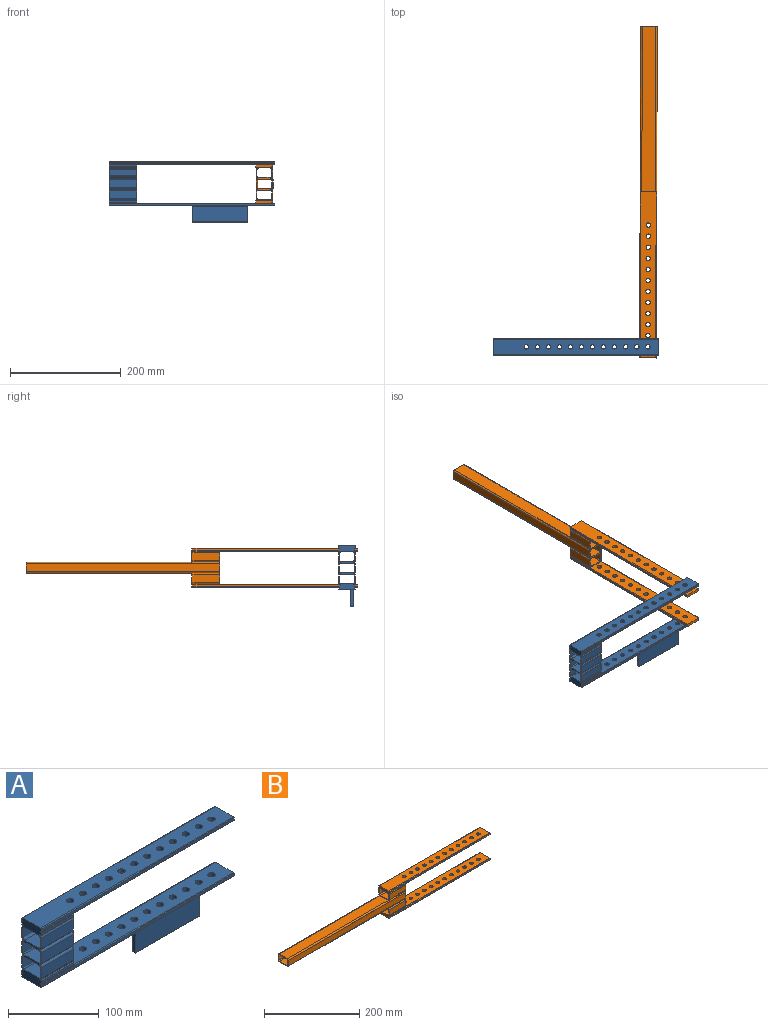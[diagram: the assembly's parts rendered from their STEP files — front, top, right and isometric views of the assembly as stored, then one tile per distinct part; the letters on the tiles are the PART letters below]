
ASSEMBLY  parts=2 mates=1
PART A: 111 faces, bbox 300x30x110 mm
  f0: cylinder r=1.5mm len=50mm, axis (-1,0,0), area 117.8mm2, adj f1,f57,f58,f59
  f1: plane 50x24mm, normal (0,0,-1), area 1200mm2, adj f0,f2,f58,f59
  f2: cylinder r=1.5mm len=50mm, axis (-1,0,0), area 117.8mm2, adj f1,f3,f58,f59
  f3: plane 50x14mm, normal (0,-1,0), area 700mm2, adj f2,f4,f58,f59
  f4: cylinder r=1.5mm len=50mm, axis (-1,0,0), area 117.8mm2, adj f3,f5,f58,f59
  f5: plane 50x24mm, normal (0,0,1), area 1200mm2, adj f4,f6,f58,f59
  f6: cylinder r=1.5mm len=50mm, axis (-1,0,0), area 117.8mm2, adj f5,f57,f58,f59
  f7: cylinder r=1.5mm len=50mm, axis (-1,0,0), area 117.8mm2, adj f8,f54,f58,f59
  f8: plane 50x24mm, normal (0,0,1), area 1200mm2, adj f7,f9,f58,f59
  f9: cylinder r=1.5mm len=50mm, axis (-1,0,0), area 117.8mm2, adj f8,f10,f58,f59
  f10: plane 50x14mm, normal (0,1,0), area 700mm2, adj f9,f11,f58,f59
  f11: cylinder r=1.5mm len=50mm, axis (-1,0,0), area 117.8mm2, adj f10,f12,f58,f59
  f12: plane 50x24mm, normal (0,0,-1), area 1200mm2, adj f11,f13,f58,f59
  f13: cylinder r=1.5mm len=50mm, axis (-1,0,0), area 117.8mm2, adj f12,f54,f58,f59
  f14: cylinder r=3mm len=50mm, axis (-1,0,0), area 235.6mm2, adj f15,f55,f58,f59
  f15: plane 50x21mm, normal (0,0,1), area 1050mm2, adj f14,f16,f58,f59
  f16: cylinder r=3mm len=50mm, axis (-1,0,0), area 235.6mm2, adj f15,f17,f58,f59
  f17: plane 50x11mm, normal (0,1,0), area 550mm2, adj f16,f18,f58,f59
  f18: cylinder r=3mm len=50mm, axis (-1,0,0), area 235.6mm2, adj f17,f19,f58,f59
  f19: plane 50x21mm, normal (0,0,-1), area 1050mm2, adj f18,f20,f58,f59
  f20: cylinder r=3mm len=50mm, axis (-1,0,0), area 235.6mm2, adj f19,f55,f58,f59
  f21: plane 50x3mm, normal (0,1,0), area 150mm2, adj f22,f56,f58,f59
  f22: cylinder r=1mm len=50mm, axis (-1,0,0), area 78.5mm2, adj f21,f58,f59,f63
  f23: cylinder r=1mm len=50mm, axis (-1,0,0), area 78.5mm2, adj f24,f58,f59,f61
  f24: plane 50x3mm, normal (0,-1,0), area 150mm2, adj f23,f25,f58,f59
  f25: cylinder r=1mm len=50mm, axis (-1,0,0), area 78.5mm2, adj f24,f26,f58,f59
  f26: plane 50x2mm, normal (0,0,-1), area 100mm2, adj f25,f27,f58,f59
  f27: cylinder r=3mm len=50mm, axis (-1,0,0), area 235.6mm2, adj f26,f28,f58,f59
  f28: plane 50x14mm, normal (0,-1,0), area 700mm2, adj f27,f29,f58,f59
  f29: cylinder r=3mm len=50mm, axis (-1,0,0), area 235.6mm2, adj f28,f30,f58,f59
  f30: cylinder r=3mm len=50mm, axis (-1,0,0), area 235.6mm2, adj f29,f31,f58,f59
  f31: plane 50x14mm, normal (0,-1,0), area 700mm2, adj f30,f32,f58,f59
  f32: cylinder r=3mm len=50mm, axis (-1,0,0), area 235.6mm2, adj f31,f33,f58,f59
  f33: cylinder r=3mm len=50mm, axis (-1,0,0), area 235.6mm2, adj f32,f34,f58,f59
  f34: plane 50x14mm, normal (0,-1,0), area 700mm2, adj f33,f35,f58,f59
  f35: cylinder r=3mm len=50mm, axis (-1,0,0), area 235.6mm2, adj f34,f36,f58,f59
  f36: plane 50x2mm, normal (0,0,1), area 100mm2, adj f35,f37,f58,f59
  f37: cylinder r=1mm len=50mm, axis (-1,0,0), area 78.5mm2, adj f36,f38,f58,f59
  f38: plane 50x3mm, normal (0,-1,0), area 150mm2, adj f37,f39,f58,f59
  f39: cylinder r=1mm len=50mm, axis (-1,0,0), area 78.5mm2, adj f38,f58,f59,f71
  f40: cylinder r=1mm len=50mm, axis (-1,0,0), area 78.5mm2, adj f41,f58,f59,f69
  f41: plane 50x3mm, normal (0,1,0), area 150mm2, adj f40,f42,f58,f59
  f42: cylinder r=1mm len=50mm, axis (-1,0,0), area 78.5mm2, adj f41,f43,f58,f59
  f43: plane 50x2mm, normal (0,0,1), area 100mm2, adj f42,f44,f58,f59
  f44: cylinder r=3mm len=50mm, axis (-1,0,0), area 235.6mm2, adj f43,f45,f58,f59
  f45: plane 50x14mm, normal (0,1,0), area 700mm2, adj f44,f46,f58,f59
  f46: cylinder r=3mm len=50mm, axis (-1,0,0), area 235.6mm2, adj f45,f47,f58,f59
  f47: cylinder r=3mm len=50mm, axis (-1,0,0), area 235.6mm2, adj f46,f48,f58,f59
  f48: plane 50x14mm, normal (0,1,0), area 700mm2, adj f47,f49,f58,f59
  f49: cylinder r=3mm len=50mm, axis (-1,0,0), area 235.6mm2, adj f48,f50,f58,f59
  f50: cylinder r=3mm len=50mm, axis (-1,0,0), area 235.6mm2, adj f49,f51,f58,f59
  f51: plane 50x14mm, normal (0,1,0), area 700mm2, adj f50,f52,f58,f59
  f52: cylinder r=3mm len=50mm, axis (-1,0,0), area 235.6mm2, adj f51,f53,f58,f59
  f53: plane 50x2mm, normal (0,0,-1), area 100mm2, adj f52,f56,f58,f59
  f54: plane 50x14mm, normal (0,-1,0), area 700mm2, adj f7,f13,f58,f59
  f55: plane 50x11mm, normal (0,-1,0), area 550mm2, adj f14,f20,f58,f59
  f56: cylinder r=1mm len=50mm, axis (-1,0,0), area 78.5mm2, adj f21,f53,f58,f59
  f57: plane 50x14mm, normal (0,1,0), area 700mm2, adj f0,f6,f58,f59
  f58: plane 70x30mm, normal (1,0,0), area 709.7mm2, adj f0,f1,f2,f3,f4,f5,f6,f7
  f59: plane 80x30mm, normal (-1,0,0), area 1008mm2, adj f0,f1,f2,f3,f4,f5,f6,f7
  f60: plane 300x3mm, normal (0,-1,0), area 900mm2, adj f59,f61,f67,f68
  f61: cylinder r=1mm len=300mm, axis (-1,0,0), area 471.2mm2, adj f23,f59,f60,f62,f68
  f62: plane 250x28mm, normal (0,0,-1), area 6396.8mm2, adj f58,f61,f63,f68,f90,f91,f92,f93
  f63: cylinder r=1mm len=300mm, axis (-1,0,0), area 471.2mm2, adj f22,f59,f62,f64,f68
  f64: plane 300x3mm, normal (0,1,0), area 900mm2, adj f59,f63,f65,f68
  f65: cylinder r=1mm len=300mm, axis (-1,0,0), area 471.2mm2, adj f59,f64,f66,f68
  f66: plane 300x28mm, normal (0,0,1), area 7796.8mm2, adj f59,f65,f67,f68,f90,f91,f92,f93
  f67: cylinder r=1mm len=300mm, axis (-1,0,0), area 471.2mm2, adj f59,f60,f66,f68
  f68: plane 30x5mm, normal (1,0,0), area 149.1mm2, adj f60,f61,f62,f63,f64,f65,f66,f67
  f69: cylinder r=1mm len=300mm, axis (-1,0,0), area 471.2mm2, adj f40,f59,f70,f76,f77
  f70: plane 250x28mm, normal (0,0,1), area 6396.8mm2, adj f58,f69,f71,f77,f78,f79,f80,f81
  f71: cylinder r=1mm len=300mm, axis (-1,0,0), area 471.2mm2, adj f39,f59,f70,f72,f77
  f72: plane 300x3mm, normal (0,-1,0), area 900mm2, adj f59,f71,f73,f77
  f73: cylinder r=1mm len=300mm, axis (-1,0,0), area 471.2mm2, adj f59,f72,f74,f77
  f74: plane 300x28mm, normal (0,0,-1), area 7496.8mm2, adj f59,f73,f75,f77,f78,f79,f80,f81
  f75: cylinder r=1mm len=300mm, axis (-1,0,0), area 471.2mm2, adj f59,f74,f76,f77
  f76: plane 300x3mm, normal (0,1,0), area 900mm2, adj f59,f69,f75,f77
  f77: plane 30x5mm, normal (1,0,0), area 149.1mm2, adj f69,f70,f71,f72,f73,f74,f75,f76
  f78: cylinder r=4mm len=8mm, axis (0,0,1), area 125.7mm2, adj f70,f74
  f79: cylinder r=4mm len=8mm, axis (0,0,1), area 125.7mm2, adj f70,f74
  f80: cylinder r=4mm len=8mm, axis (0,0,1), area 125.7mm2, adj f70,f74
  f81: cylinder r=4mm len=8mm, axis (0,0,1), area 125.7mm2, adj f70,f74
  f82: cylinder r=4mm len=8mm, axis (0,0,1), area 125.7mm2, adj f70,f74
  f83: cylinder r=4mm len=8mm, axis (0,0,1), area 125.7mm2, adj f70,f74
  f84: cylinder r=4mm len=8mm, axis (0,0,1), area 125.7mm2, adj f70,f74
  f85: cylinder r=4mm len=8mm, axis (0,0,1), area 125.7mm2, adj f70,f74
  f86: cylinder r=4mm len=8mm, axis (0,0,1), area 125.7mm2, adj f70,f74
  f87: cylinder r=4mm len=8mm, axis (0,0,1), area 125.7mm2, adj f70,f74
  f88: cylinder r=4mm len=8mm, axis (0,0,1), area 125.7mm2, adj f70,f74
  f89: cylinder r=4mm len=8mm, axis (0,0,1), area 125.7mm2, adj f70,f74
  f90: cylinder r=4mm len=8mm, axis (0,0,1), area 125.7mm2, adj f62,f66
  f91: cylinder r=4mm len=8mm, axis (0,0,1), area 125.7mm2, adj f62,f66
  f92: cylinder r=4mm len=8mm, axis (0,0,1), area 125.7mm2, adj f62,f66
  f93: cylinder r=4mm len=8mm, axis (0,0,1), area 125.7mm2, adj f62,f66
  f94: cylinder r=4mm len=8mm, axis (0,0,1), area 125.7mm2, adj f62,f66
  f95: cylinder r=4mm len=8mm, axis (0,0,1), area 125.7mm2, adj f62,f66
  f96: cylinder r=4mm len=8mm, axis (0,0,1), area 125.7mm2, adj f62,f66
  f97: cylinder r=4mm len=8mm, axis (0,0,1), area 125.7mm2, adj f62,f66
  f98: cylinder r=4mm len=8mm, axis (0,0,1), area 125.7mm2, adj f62,f66
  f99: cylinder r=4mm len=8mm, axis (0,0,1), area 125.7mm2, adj f62,f66
  f100: cylinder r=4mm len=8mm, axis (0,0,1), area 125.7mm2, adj f62,f66
  f101: cylinder r=4mm len=8mm, axis (0,0,1), area 125.7mm2, adj f62,f66
  f102: plane 100x3mm, normal (0,0,-1), area 300mm2, adj f103,f108,f109,f110
  f103: cylinder r=1mm len=100mm, axis (-1,0,0), area 157.1mm2, adj f102,f104,f109,f110
  f104: plane 100x28mm, normal (0,1,0), area 2800mm2, adj f103,f105,f109,f110
  f105: cylinder r=1mm len=100mm, axis (-1,0,0), area 157.1mm2, adj f74,f104,f109,f110
  f106: cylinder r=1mm len=100mm, axis (-1,0,0), area 157.1mm2, adj f74,f107,f109,f110
  f107: plane 100x28mm, normal (0,-1,0), area 2800mm2, adj f106,f108,f109,f110
  f108: cylinder r=1mm len=100mm, axis (-1,0,0), area 157.1mm2, adj f102,f107,f109,f110
  f109: plane 30x5mm, normal (1,0,0), area 149.1mm2, adj f74,f102,f103,f104,f105,f106,f107,f108
  f110: plane 30x5mm, normal (-1,0,0), area 149.1mm2, adj f74,f102,f103,f104,f105,f106,f107,f108
PART B: 90 faces, bbox 600x30x70 mm
  f0: plane 300x24mm, normal (0,0,-1), area 7200mm2, adj f5,f6,f17,f47
  f1: plane 300x24mm, normal (0,0,1), area 7200mm2, adj f2,f3,f17,f32
  f2: cylinder r=3mm len=350mm, axis (-1,0,0), area 1649.3mm2, adj f1,f15,f16,f17,f25
  f3: cylinder r=3mm len=350mm, axis (-1,0,0), area 1649.3mm2, adj f1,f4,f16,f17,f30
  f4: plane 350x14mm, normal (0,-1,0), area 4900mm2, adj f3,f5,f16,f17
  f5: cylinder r=3mm len=350mm, axis (-1,0,0), area 1649.3mm2, adj f0,f4,f16,f17,f34
  f6: cylinder r=3mm len=350mm, axis (-1,0,0), area 1649.3mm2, adj f0,f15,f16,f17,f33
  f7: cylinder r=1.5mm len=350mm, axis (-1,0,0), area 824.7mm2, adj f8,f14,f16,f17
  f8: plane 350x24mm, normal (0,0,1), area 8400mm2, adj f7,f9,f16,f17
  f9: cylinder r=1.5mm len=350mm, axis (-1,0,0), area 824.7mm2, adj f8,f10,f16,f17
  f10: plane 350x14mm, normal (0,1,0), area 4900mm2, adj f9,f11,f16,f17
  f11: cylinder r=1.5mm len=350mm, axis (-1,0,0), area 824.7mm2, adj f10,f12,f16,f17
  f12: plane 350x24mm, normal (0,0,-1), area 8400mm2, adj f11,f13,f16,f17
  f13: cylinder r=1.5mm len=350mm, axis (-1,0,0), area 824.7mm2, adj f12,f14,f16,f17
  f14: plane 350x14mm, normal (0,-1,0), area 4900mm2, adj f7,f13,f16,f17
  f15: plane 350x14mm, normal (0,1,0), area 4900mm2, adj f2,f6,f16,f17
  f16: plane 60x30mm, normal (1,0,0), area 411.4mm2, adj f2,f3,f4,f5,f6,f7,f8,f9
  f17: plane 30x20mm, normal (-1,0,0), area 135.2mm2, adj f0,f1,f2,f3,f4,f5,f6,f7
  f18: cylinder r=3mm len=50mm, axis (-1,0,0), area 235.6mm2, adj f16,f19,f31,f32
  f19: plane 50x21mm, normal (0,0,1), area 1050mm2, adj f16,f18,f20,f32
  f20: cylinder r=3mm len=50mm, axis (-1,0,0), area 235.6mm2, adj f16,f19,f21,f32
  f21: plane 50x11mm, normal (0,1,0), area 550mm2, adj f16,f20,f22,f32
  f22: cylinder r=3mm len=50mm, axis (-1,0,0), area 235.6mm2, adj f16,f21,f23,f32
  f23: plane 50x21mm, normal (0,0,-1), area 1050mm2, adj f16,f22,f24,f32
  f24: cylinder r=3mm len=50mm, axis (-1,0,0), area 235.6mm2, adj f16,f23,f31,f32
  f25: cylinder r=3mm len=50mm, axis (-1,0,0), area 235.6mm2, adj f2,f16,f26,f32
  f26: plane 50x14mm, normal (0,1,0), area 700mm2, adj f16,f25,f27,f32
  f27: cylinder r=3mm len=50mm, axis (-1,0,0), area 235.6mm2, adj f16,f26,f32,f48
  f28: cylinder r=3mm len=50mm, axis (-1,0,0), area 235.6mm2, adj f16,f29,f32,f48
  f29: plane 50x14mm, normal (0,-1,0), area 700mm2, adj f16,f28,f30,f32
  f30: cylinder r=3mm len=50mm, axis (-1,0,0), area 235.6mm2, adj f3,f16,f29,f32
  f31: plane 50x11mm, normal (0,-1,0), area 550mm2, adj f16,f18,f24,f32
  f32: plane 30x25mm, normal (-1,0,0), area 290.1mm2, adj f1,f18,f19,f20,f21,f22,f23,f24
  f33: cylinder r=3mm len=50mm, axis (-1,0,0), area 235.6mm2, adj f6,f16,f46,f47
  f34: cylinder r=3mm len=50mm, axis (-1,0,0), area 235.6mm2, adj f5,f16,f35,f47
  f35: plane 50x14mm, normal (0,-1,0), area 700mm2, adj f16,f34,f36,f47
  f36: cylinder r=3mm len=50mm, axis (-1,0,0), area 235.6mm2, adj f16,f35,f47,f57
  f37: cylinder r=3mm len=50mm, axis (-1,0,0), area 235.6mm2, adj f16,f46,f47,f57
  f38: cylinder r=1.5mm len=50mm, axis (-1,0,0), area 117.8mm2, adj f16,f39,f45,f47
  f39: plane 50x24mm, normal (0,0,-1), area 1200mm2, adj f16,f38,f40,f47
  f40: cylinder r=1.5mm len=50mm, axis (-1,0,0), area 117.8mm2, adj f16,f39,f41,f47
  f41: plane 50x14mm, normal (0,-1,0), area 700mm2, adj f16,f40,f42,f47
  f42: cylinder r=1.5mm len=50mm, axis (-1,0,0), area 117.8mm2, adj f16,f41,f43,f47
  f43: plane 50x24mm, normal (0,0,1), area 1200mm2, adj f16,f42,f44,f47
  f44: cylinder r=1.5mm len=50mm, axis (-1,0,0), area 117.8mm2, adj f16,f43,f45,f47
  f45: plane 50x14mm, normal (0,1,0), area 700mm2, adj f16,f38,f44,f47
  f46: plane 50x14mm, normal (0,1,0), area 700mm2, adj f16,f33,f37,f47
  f47: plane 30x25mm, normal (-1,0,0), area 284.3mm2, adj f0,f33,f34,f35,f36,f37,f38,f39
  f48: plane 300x28mm, normal (0,0,-1), area 6596.8mm2, adj f16,f27,f28,f32,f49,f55,f56,f78
  f49: cylinder r=1mm len=300mm, axis (-1,0,0), area 471.2mm2, adj f32,f48,f50,f56
  f50: plane 300x3mm, normal (0,1,0), area 900mm2, adj f32,f49,f51,f56
  f51: cylinder r=1mm len=300mm, axis (-1,0,0), area 471.2mm2, adj f32,f50,f52,f56
  f52: plane 300x28mm, normal (0,0,1), area 7796.8mm2, adj f32,f51,f53,f56,f78,f79,f80,f81
  f53: cylinder r=1mm len=300mm, axis (-1,0,0), area 471.2mm2, adj f32,f52,f54,f56
  f54: plane 300x3mm, normal (0,-1,0), area 900mm2, adj f32,f53,f55,f56
  f55: cylinder r=1mm len=300mm, axis (-1,0,0), area 471.2mm2, adj f32,f48,f54,f56
  f56: plane 30x5mm, normal (1,0,0), area 149.1mm2, adj f48,f49,f50,f51,f52,f53,f54,f55
  f57: plane 300x28mm, normal (0,0,1), area 6596.8mm2, adj f16,f36,f37,f47,f58,f64,f65,f66
  f58: cylinder r=1mm len=300mm, axis (-1,0,0), area 471.2mm2, adj f47,f57,f59,f65
  f59: plane 300x3mm, normal (0,-1,0), area 900mm2, adj f47,f58,f60,f65
  f60: cylinder r=1mm len=300mm, axis (-1,0,0), area 471.2mm2, adj f47,f59,f61,f65
  f61: plane 300x28mm, normal (0,0,-1), area 7796.8mm2, adj f47,f60,f62,f65,f66,f67,f68,f69
  f62: cylinder r=1mm len=300mm, axis (-1,0,0), area 471.2mm2, adj f47,f61,f63,f65
  f63: plane 300x3mm, normal (0,1,0), area 900mm2, adj f47,f62,f64,f65
  f64: cylinder r=1mm len=300mm, axis (-1,0,0), area 471.2mm2, adj f47,f57,f63,f65
  f65: plane 30x5mm, normal (1,0,0), area 149.1mm2, adj f57,f58,f59,f60,f61,f62,f63,f64
  f66: cylinder r=4mm len=8mm, axis (0,0,1), area 125.7mm2, adj f57,f61
  f67: cylinder r=4mm len=8mm, axis (0,0,1), area 125.7mm2, adj f57,f61
  f68: cylinder r=4mm len=8mm, axis (0,0,1), area 125.7mm2, adj f57,f61
  f69: cylinder r=4mm len=8mm, axis (0,0,1), area 125.7mm2, adj f57,f61
  f70: cylinder r=4mm len=8mm, axis (0,0,1), area 125.7mm2, adj f57,f61
  f71: cylinder r=4mm len=8mm, axis (0,0,1), area 125.7mm2, adj f57,f61
  f72: cylinder r=4mm len=8mm, axis (0,0,1), area 125.7mm2, adj f57,f61
  f73: cylinder r=4mm len=8mm, axis (0,0,1), area 125.7mm2, adj f57,f61
  f74: cylinder r=4mm len=8mm, axis (0,0,1), area 125.7mm2, adj f57,f61
  f75: cylinder r=4mm len=8mm, axis (0,0,1), area 125.7mm2, adj f57,f61
  f76: cylinder r=4mm len=8mm, axis (0,0,1), area 125.7mm2, adj f57,f61
  f77: cylinder r=4mm len=8mm, axis (0,0,1), area 125.7mm2, adj f57,f61
  f78: cylinder r=4mm len=8mm, axis (0,0,1), area 125.7mm2, adj f48,f52
  f79: cylinder r=4mm len=8mm, axis (0,0,1), area 125.7mm2, adj f48,f52
  f80: cylinder r=4mm len=8mm, axis (0,0,1), area 125.7mm2, adj f48,f52
  f81: cylinder r=4mm len=8mm, axis (0,0,1), area 125.7mm2, adj f48,f52
  f82: cylinder r=4mm len=8mm, axis (0,0,1), area 125.7mm2, adj f48,f52
  f83: cylinder r=4mm len=8mm, axis (0,0,1), area 125.7mm2, adj f48,f52
  f84: cylinder r=4mm len=8mm, axis (0,0,1), area 125.7mm2, adj f48,f52
  f85: cylinder r=4mm len=8mm, axis (0,0,1), area 125.7mm2, adj f48,f52
  f86: cylinder r=4mm len=8mm, axis (0,0,1), area 125.7mm2, adj f48,f52
  f87: cylinder r=4mm len=8mm, axis (0,0,1), area 125.7mm2, adj f48,f52
  f88: cylinder r=4mm len=8mm, axis (0,0,1), area 125.7mm2, adj f48,f52
  f89: cylinder r=4mm len=8mm, axis (0,0,1), area 125.7mm2, adj f48,f52
PLACE A t=(-40.8,37.2,-23.78)mm fixed
PLACE B rot(axis=(0,0,-1),90.2deg) t=(240.14,317.19,-23.78)mm
MATE revolute A.f89 <-> B.f77  axis (0,0,1) through (239.2,37.2,-58.78)mm
